# Revit family: Kessel 9151010D en
name_source: partatom
category: Plumbing Fixtures
revit_build: Autodesk Revit Architecture 2014 (Build: 20130308_1515(x64)
units: mm (PartAtom-declared; Revit-internal decimal feet)

## types (1)
- Kessel 9151010D en
    <1.010.00.2> Number of the part of the guideline = 98
    <1.010.00.3> Issue date (month) of the guideline = 200601
    <1.010.00.4> Manufacturer name = Kessel
    <1.010.00.5> Revision date of the file = 20190227
    <1.800.00.3> BS number = 10000100000000000000000000000000000000000000000032000
    <1.800.00.4> Comment field = Sampling device CO 1000, DN100, Class D
    <1.810.00.3> Manufacturer’s reference number = 9151010D
    <1.810.00.4> DATANORM number = 9151010D
    <1.960/3L.00.8> Link (URL) = http://www.kessel.de
    <98.100.00.4> Area of application = Accessories
    <98.110.00.4> Product series = Accessories
    <98.700.00.4> Product name = Sampling device CO 1000, DN100, Class D
    CONNECTOR0_DIAMETER_dX_0r = 0 mm  [stored 0 ft]
    CONNECTOR0_dX_00 = 547 mm
    CONNECTOR0_dX_01 = 370 mm
    CONNECTOR0_ref_dX = 370 mm
    CONNECTOR1_DIAMETER_dNBN0_0r = 0 mm  [stored 0 ft]
    CONNECTOR1_dNBN0_00 = 518 mm
    CONNECTOR1_dNBN0_01 = 632 mm
    CONNECTOR1_ref_dNBN0 = 518 mm
    CONNECTOR1_ref_dNBN1 = 174 mm
    Manufacturer = Kessel
    Model = 9151010D
    URL = www.kessel.com

note: [stored X ft] marks values corroborated as IEEE doubles in the binary element streams (Revit-internal decimal feet)
